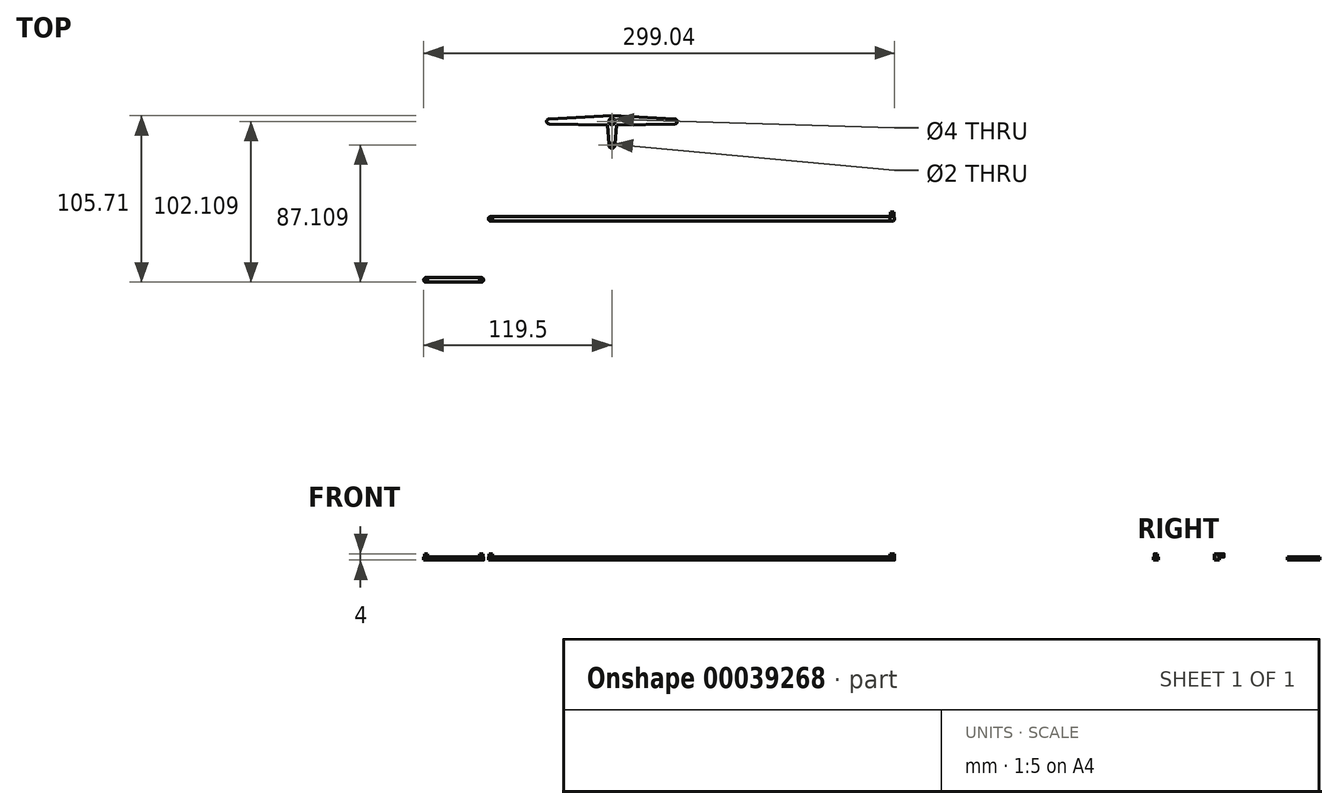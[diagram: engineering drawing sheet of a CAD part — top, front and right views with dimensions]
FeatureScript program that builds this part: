
annotation { "Feature Type Name" : "Feature", "Feature Type Description" : "" }
export const myFeature = defineFeature(function(context is Context, id is Id, definition is map)
    precondition{}
    {
        {
            var Q0;
            Q0=qCreatedBy(makeId("Top.planeOp"),FACE);
            var sketch = newSketch(context, id + "F0", { "sketchPlane" : qUnion([Q0])});
            skCircle(sketch, "E0", {"center": v(-58.59, -38.75) * mm, "radius": 1 * mm});
            skCircle(sketch, "E1", {"center": v(-58.59, -38.75) * mm, "radius": 1.48 * mm});
            skLineSegment(sketch, "E2", {"start": v(-58.59, -38.75) * mm, "end": v(-23.59, -38.75) * mm});
            skCircle(sketch, "E3", {"center": v(-23.59, -38.75) * mm, "radius": 1 * mm});
            skCircle(sketch, "E4", {"center": v(-23.59, -38.75) * mm, "radius": 1.48 * mm});
            skLineSegment(sketch, "E5", {"start": v(-58.58, -37.26) * mm, "end": v(-23.59, -37.26) * mm});
            skLineSegment(sketch, "E6", {"start": v(-58.37, -40.22) * mm, "end": v(-23.59, -40.23) * mm});
            skSolve(sketch);
        }
        {
            var Q0;
            Q0=makeQuery(id+"F0.imprint","IMPRINT",FACE,{"disambiguationData":[TD([[makeQuery(id+"F0.imprint","IMPRINT",EDGE,{"derivedFrom":sQuery(id+"F0.wireOp",EDGE,"E0")}),1.0]])]});
            var Q1;
            Q1=makeQuery(id+"F0.imprint","IMPRINT",FACE,{"disambiguationData":[TD([[makeQuery(id+"F0.imprint","IMPRINT",EDGE,{"derivedFrom":sQuery(id+"F0.wireOp",EDGE,"E3")}),1.0]])]});
            extrude(context, id + "F1", {"entities" : qUnion([Q0, Q1]), "depth" : 4 * mm});
        }
        {
            var Q0;
            {var subQ0=sQuery(id+"F0.wireOp",EDGE,"E5");Q0=makeQuery(id+"F0.imprint","IMPRINT",FACE,{"disambiguationData":[TD([[makeQuery(id+"F0.imprint","IMPRINT",EDGE,{"derivedFrom":subQ0}),-1.0]])]});}
            var Q1;
            {var subQ0=sQuery(id+"F0.wireOp",EDGE,"E6");Q1=makeQuery(id+"F0.imprint","IMPRINT",FACE,{"disambiguationData":[TD([[makeQuery(id+"F0.imprint","IMPRINT",EDGE,{"derivedFrom":subQ0}),1.0]])]});}
            var Q2;
            Q2=makeQuery(id+"F0.imprint","IMPRINT",FACE,{"disambiguationData":[TD([[makeQuery(id+"F0.imprint","IMPRINT",EDGE,{"derivedFrom":sQuery(id+"F0.wireOp",EDGE,"E3")}),-1.0]])]});
            var Q3;
            Q3=makeQuery(id+"F0.imprint","IMPRINT",FACE,{"disambiguationData":[TD([[makeQuery(id+"F0.imprint","IMPRINT",EDGE,{"derivedFrom":sQuery(id+"F0.wireOp",EDGE,"E0")}),-1.0]])]});
            extrude(context, id + "F2", {"entities" : qUnion([Q0, Q1, Q2, Q3]), "operationType" : NewBodyOperationType.ADD, "depth" : 2 * mm});
        }
        {
            var Q0;
            Q0=qCreatedBy(makeId("Top.planeOp"),FACE);
            var sketch = newSketch(context, id + "F3", { "sketchPlane" : qUnion([Q0])});
            skCircle(sketch, "E7", {"center": v(-17.52, 0) * mm, "radius": 1 * mm});
            skCircle(sketch, "E8", {"center": v(-17.52, 0) * mm, "radius": 1.48 * mm});
            skLineSegment(sketch, "E9", {"start": v(-17.52, 0) * mm, "end": v(237.48, 0) * mm});
            skCircle(sketch, "E10", {"center": v(237.48, 0) * mm, "radius": 1 * mm});
            skCircle(sketch, "E11", {"center": v(237.48, 0) * mm, "radius": 1.48 * mm});
            skLineSegment(sketch, "E12", {"start": v(-17.5, 1.48) * mm, "end": v(237.48, 1.48) * mm});
            skLineSegment(sketch, "E13", {"start": v(-17.3, -1.47) * mm, "end": v(237.48, -1.49) * mm});
            skSolve(sketch);
        }
        {
            var Q0;
            Q0=makeQuery(id+"F3.imprint","IMPRINT",FACE,{"disambiguationData":[TD([[makeQuery(id+"F3.imprint","IMPRINT",EDGE,{"derivedFrom":sQuery(id+"F3.wireOp",EDGE,"E7")}),1.0]])]});
            var Q1;
            Q1=makeQuery(id+"F3.imprint","IMPRINT",FACE,{"disambiguationData":[TD([[makeQuery(id+"F3.imprint","IMPRINT",EDGE,{"derivedFrom":sQuery(id+"F3.wireOp",EDGE,"E10")}),-1.0]])]});
            var Q2;
            Q2=makeQuery(id+"F3.imprint","IMPRINT",FACE,{"disambiguationData":[TD([[makeQuery(id+"F3.imprint","IMPRINT",EDGE,{"derivedFrom":sQuery(id+"F3.wireOp",EDGE,"E10")}),1.0]])]});
            extrude(context, id + "F4", {"entities" : qUnion([Q0, Q1, Q2]), "depth" : 4 * mm});
        }
        {
            var Q0;
            {var subQ0=sQuery(id+"F3.wireOp",EDGE,"E12");Q0=makeQuery(id+"F3.imprint","IMPRINT",FACE,{"disambiguationData":[TD([[makeQuery(id+"F3.imprint","IMPRINT",EDGE,{"derivedFrom":subQ0}),-1.0]])]});}
            var Q1;
            {var subQ0=sQuery(id+"F3.wireOp",EDGE,"E13");Q1=makeQuery(id+"F3.imprint","IMPRINT",FACE,{"disambiguationData":[TD([[makeQuery(id+"F3.imprint","IMPRINT",EDGE,{"derivedFrom":subQ0}),1.0]])]});}
            var Q2;
            Q2=makeQuery(id+"F3.imprint","IMPRINT",FACE,{"disambiguationData":[TD([[makeQuery(id+"F3.imprint","IMPRINT",EDGE,{"derivedFrom":sQuery(id+"F3.wireOp",EDGE,"E7")}),-1.0]])]});
            extrude(context, id + "F5", {"entities" : qUnion([Q0, Q1, Q2]), "operationType" : NewBodyOperationType.ADD, "depth" : 2 * mm});
        }
        {
            var Q0;
            Q0=makeQuery(id+"F5.opExtrude","SWEPT_FACE",FACE,{"disambiguationData":[OSD([sQuery(id+"F3.wireOp",EDGE,"E12")])]});
            var sketch = newSketch(context, id + "F6", { "sketchPlane" : qUnion([Q0])});
            skLineSegment(sketch, "E14", {"start": v(-237.48, 2) * mm, "end": v(-237.48, 3) * mm});
            skCircle(sketch, "E15", {"center": v(-237.48, 3) * mm, "radius": 1 * mm});
            skSolve(sketch);
        }
        {
            var Q0;
            Q0=makeQuery(id+"F6.imprint","IMPRINT",FACE,{"disambiguationData":[TD([[makeQuery(id+"F6.imprint","IMPRINT",EDGE,{"derivedFrom":sQuery(id+"F6.wireOp",EDGE,"E15")}),1.0]])]});
            extrude(context, id + "F7", {"entities" : qUnion([Q0]), "operationType" : NewBodyOperationType.ADD, "oppositeDirection" : true, "depth" : 2 * mm});
        }
        {
            var Q0;
            Q0=makeQuery(id+"F7.opExtrude","CAP_FACE",FACE,{"disambiguationData":[OSD([sQuery(id+"F6.wireOp",EDGE,"E15")])],"isStart":true});
            extrude(context, id + "F8", {"entities" : qUnion([Q0]), "operationType" : NewBodyOperationType.ADD, "depth" : 3 * mm});
        }
        {
            var Q0;
            Q0=qCreatedBy(makeId("Top.planeOp"),FACE);
            var sketch = newSketch(context, id + "F9", { "sketchPlane" : qUnion([Q0])});
            skCircle(sketch, "E16", {"center": v(59.43, 46.88) * mm, "radius": 1 * mm});
            skCircle(sketch, "E17", {"center": v(59.43, 46.88) * mm, "radius": 2 * mm});
            skLineSegment(sketch, "E18", {"start": v(59.43, 46.88) * mm, "end": v(59.43, 61.88) * mm});
            skCircle(sketch, "E19", {"center": v(59.43, 61.88) * mm, "radius": 2 * mm});
            skLineSegment(sketch, "E20", {"start": v(59.43, 61.88) * mm, "end": v(99.43, 61.88) * mm});
            skLineSegment(sketch, "E21", {"start": v(59.43, 61.88) * mm, "end": v(19.43, 61.88) * mm});
            skCircle(sketch, "E22", {"center": v(59.43, 61.88) * mm, "radius": 3.6 * mm});
            skLineSegment(sketch, "E23", {"start": v(57.53, 47.5) * mm, "end": v(56.57, 59.69) * mm});
            skLineSegment(sketch, "E24", {"start": v(61.33, 47.5) * mm, "end": v(62.29, 59.69) * mm});
            skCircle(sketch, "E25", {"center": v(19.43, 61.88) * mm, "radius": 1.5 * mm});
            skCircle(sketch, "E26", {"center": v(99.43, 61.88) * mm, "radius": 1.5 * mm});
            skLineSegment(sketch, "E27", {"start": v(62.29, 59.69) * mm, "end": v(99.46, 60.38) * mm});
            skLineSegment(sketch, "E28", {"start": v(99.26, 63.37) * mm, "end": v(59.43, 65.48) * mm});
            skLineSegment(sketch, "E29", {"start": v(59.43, 65.48) * mm, "end": v(19.35, 63.38) * mm});
            skLineSegment(sketch, "E30", {"start": v(56.57, 59.69) * mm, "end": v(19.4, 60.38) * mm});
            skSolve(sketch);
        }
        {
            var Q0;
            {var subQ3=sQuery(id+"F9.wireOp",EDGE,"E26");var subQ5=sQuery(id+"F9.wireOp",EDGE,"E20");var subQ6=makeQuery(id+"F9.imprint","INTERSECT",VERTEX,{"derivedFrom":[subQ5,subQ3]});Q0=makeQuery(id+"F9.imprint","IMPRINT",FACE,{"disambiguationData":[TD([[makeQuery(id+"F9.imprint","IMPRINT",EDGE,{"disambiguationData":[TD([[subQ6,1.0]])],"derivedFrom":subQ5}),1.0]])]});}
            var Q1;
            {var subQ0=sQuery(id+"F9.wireOp",EDGE,"E27");Q1=makeQuery(id+"F9.imprint","IMPRINT",FACE,{"disambiguationData":[TD([[makeQuery(id+"F9.imprint","IMPRINT",EDGE,{"derivedFrom":subQ0}),1.0]])]});}
            var Q2;
            {var subQ0=sQuery(id+"F9.wireOp",EDGE,"E26");var subQ1=makeQuery(id+"F9.imprint","INTERSECT",VERTEX,{"derivedFrom":[subQ0,sQuery(id+"F9.wireOp",EDGE,"E28")]});Q2=makeQuery(id+"F9.imprint","IMPRINT",FACE,{"disambiguationData":[TD([[makeQuery(id+"F9.imprint","IMPRINT",EDGE,{"disambiguationData":[TD([[subQ1,-1.0]])],"derivedFrom":subQ0}),1.0]])]});}
            var Q3;
            {var subQ6=sQuery(id+"F9.wireOp",EDGE,"E19");var subQ9=sQuery(id+"F9.wireOp",EDGE,"E21");var subQ10=makeQuery(id+"F9.imprint","INTERSECT",VERTEX,{"derivedFrom":[subQ6,subQ9]});Q3=makeQuery(id+"F9.imprint","IMPRINT",FACE,{"disambiguationData":[TD([[makeQuery(id+"F9.imprint","IMPRINT",EDGE,{"disambiguationData":[TD([[subQ10,1.0]])],"derivedFrom":subQ6}),-1.0]])]});}
            var Q4;
            {var subQ0=sQuery(id+"F9.wireOp",EDGE,"E22");var subQ4=sQuery(id+"F9.wireOp",EDGE,"E18");var subQ7=makeQuery(id+"F9.imprint","INTERSECT",VERTEX,{"derivedFrom":[subQ4,subQ0]});Q4=makeQuery(id+"F9.imprint","IMPRINT",FACE,{"disambiguationData":[TD([[makeQuery(id+"F9.imprint","IMPRINT",EDGE,{"disambiguationData":[TD([[subQ7,-1.0]])],"derivedFrom":subQ4}),-1.0]])]});}
            var Q5;
            {var subQ0=sQuery(id+"F9.wireOp",EDGE,"E22");var subQ1=sQuery(id+"F9.wireOp",EDGE,"E18");var subQ2=makeQuery(id+"F9.imprint","INTERSECT",VERTEX,{"derivedFrom":[subQ1,subQ0]});Q5=makeQuery(id+"F9.imprint","IMPRINT",FACE,{"disambiguationData":[TD([[makeQuery(id+"F9.imprint","IMPRINT",EDGE,{"disambiguationData":[TD([[subQ2,-1.0]])],"derivedFrom":subQ1}),1.0]])]});}
            var Q6;
            {var subQ0=sQuery(id+"F9.wireOp",EDGE,"E24");Q6=makeQuery(id+"F9.imprint","IMPRINT",FACE,{"disambiguationData":[TD([[makeQuery(id+"F9.imprint","IMPRINT",EDGE,{"derivedFrom":subQ0}),1.0]])]});}
            var Q7;
            {var subQ0=sQuery(id+"F9.wireOp",EDGE,"E23");Q7=makeQuery(id+"F9.imprint","IMPRINT",FACE,{"disambiguationData":[TD([[makeQuery(id+"F9.imprint","IMPRINT",EDGE,{"derivedFrom":subQ0}),-1.0]])]});}
            var Q8;
            Q8=makeQuery(id+"F9.imprint","IMPRINT",FACE,{"disambiguationData":[TD([[makeQuery(id+"F9.imprint","IMPRINT",EDGE,{"derivedFrom":sQuery(id+"F9.wireOp",EDGE,"E16")}),-1.0]])]});
            var Q9;
            {var subQ1=sQuery(id+"F9.wireOp",EDGE,"E21");var subQ5=sQuery(id+"F9.wireOp",EDGE,"E25");var subQ7=makeQuery(id+"F9.imprint","INTERSECT",VERTEX,{"derivedFrom":[subQ1,subQ5]});Q9=makeQuery(id+"F9.imprint","IMPRINT",FACE,{"disambiguationData":[TD([[makeQuery(id+"F9.imprint","IMPRINT",EDGE,{"disambiguationData":[TD([[subQ7,1.0]])],"derivedFrom":subQ1}),-1.0]])]});}
            var Q10;
            {var subQ3=sQuery(id+"F9.wireOp",EDGE,"E30");Q10=makeQuery(id+"F9.imprint","IMPRINT",FACE,{"disambiguationData":[TD([[makeQuery(id+"F9.imprint","IMPRINT",EDGE,{"derivedFrom":subQ3}),-1.0]])]});}
            var Q11;
            {var subQ0=sQuery(id+"F9.wireOp",EDGE,"E25");var subQ3=makeQuery(id+"F9.imprint","INTERSECT",VERTEX,{"derivedFrom":[subQ0,sQuery(id+"F9.wireOp",EDGE,"E29")]});Q11=makeQuery(id+"F9.imprint","IMPRINT",FACE,{"disambiguationData":[TD([[makeQuery(id+"F9.imprint","IMPRINT",EDGE,{"disambiguationData":[TD([[subQ3,1.0]])],"derivedFrom":subQ0}),1.0]])]});}
            extrude(context, id + "F10", {"entities" : qUnion([Q0, Q1, Q2, Q3, Q4, Q5, Q6, Q7, Q8, Q9, Q10, Q11]), "depth" : 2 * mm});
        }
    });
